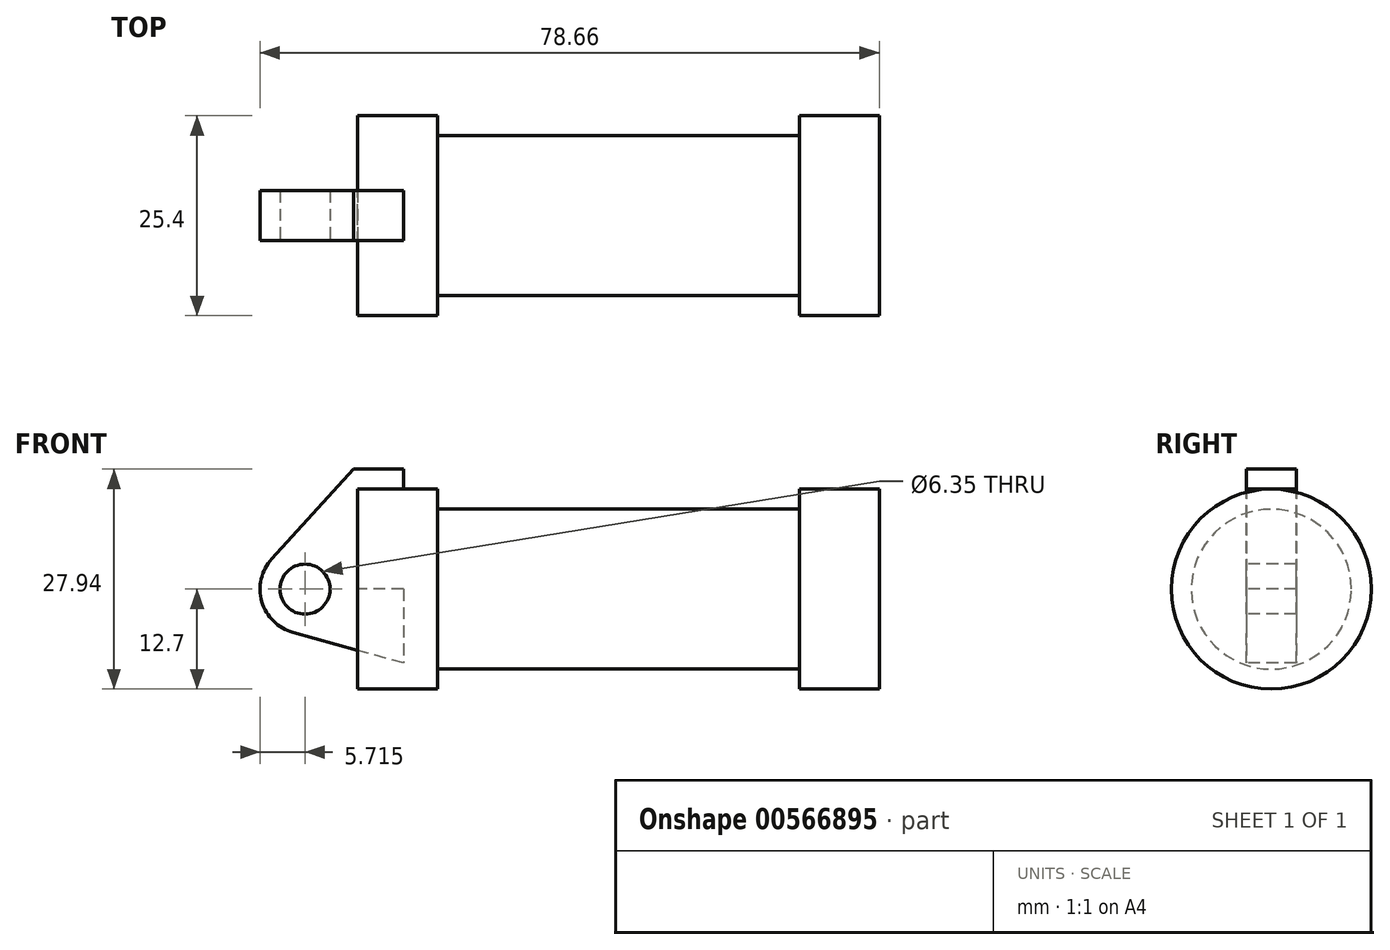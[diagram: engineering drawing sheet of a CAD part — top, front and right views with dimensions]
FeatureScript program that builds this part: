
annotation { "Feature Type Name" : "Feature", "Feature Type Description" : "" }
export const myFeature = defineFeature(function(context is Context, id is Id, definition is map)
    precondition{}
    {
        {
            var Q0;
            Q0=qCreatedBy(makeId("Front.planeOp"),FACE);
            var sketch = newSketch(context, id + "F0", { "sketchPlane" : qUnion([Q0])});
            skLineSegment(sketch, "E0", {"start": v(0, 0) * mm, "end": v(0, 12.7) * mm});
            skLineSegment(sketch, "E1", {"start": v(0, 12.7) * mm, "end": v(10.16, 12.7) * mm});
            skLineSegment(sketch, "E2", {"start": v(10.16, 12.7) * mm, "end": v(10.16, 10.16) * mm});
            skLineSegment(sketch, "E3", {"start": v(10.16, 10.16) * mm, "end": v(56.13, 10.16) * mm});
            skLineSegment(sketch, "E4", {"start": v(56.13, 10.16) * mm, "end": v(56.13, 12.7) * mm});
            skLineSegment(sketch, "E5", {"start": v(56.13, 12.7) * mm, "end": v(66.3, 12.7) * mm});
            skLineSegment(sketch, "E6", {"start": v(66.3, 12.7) * mm, "end": v(66.3, 0) * mm});
            skLineSegment(sketch, "E7", {"start": v(66.3, 0) * mm, "end": v(0, 0) * mm});
            skLineSegment(sketch, "E8", {"start": v(5.84, 15.24) * mm, "end": v(-0.5, 15.24) * mm});
            skLineSegment(sketch, "E9", {"start": v(-0.5, 15.24) * mm, "end": v(-10.88, 3.85) * mm});
            skLineSegment(sketch, "E10", {"start": v(0, 0) * mm, "end": v(-6.65, 0) * mm});
            skCircle(sketch, "E11", {"center": v(-6.65, 0) * mm, "radius": 5.72 * mm});
            skCircle(sketch, "E12", {"center": v(-6.65, 0) * mm, "radius": 3.18 * mm});
            skLineSegment(sketch, "E13", {"start": v(5.84, 15.24) * mm, "end": v(5.84, -9.4) * mm});
            skLineSegment(sketch, "E14", {"start": v(5.84, -9.4) * mm, "end": v(-8.18, -5.5) * mm});
            skSolve(sketch);
        }
        {
            var Q0;
            {var subQ0=sQuery(id+"F0.wireOp",EDGE,"E0");Q0=makeQuery(id+"F0.imprint","IMPRINT",FACE,{"disambiguationData":[TD([[makeQuery(id+"F0.imprint","IMPRINT",EDGE,{"derivedFrom":subQ0}),-1.0]])]});}
            var Q1;
            {var subQ0=sQuery(id+"F0.wireOp",EDGE,"E2");Q1=makeQuery(id+"F0.imprint","IMPRINT",FACE,{"disambiguationData":[TD([[makeQuery(id+"F0.imprint","IMPRINT",EDGE,{"derivedFrom":subQ0}),-1.0]])]});}
            var Q2;
            Q2=sQuery(id+"F0.wireOp",EDGE,"E7");
            revolve(context, id + "F1", {"entities" : qUnion([Q0, Q1]), "axis" : qUnion([Q2]), "revolveType" : RevolveType.FULL});
        }
        {
            var Q0;
            {var subQ1=sQuery(id+"F0.wireOp",EDGE,"E0");Q0=makeQuery(id+"F0.imprint","IMPRINT",FACE,{"disambiguationData":[TD([[makeQuery(id+"F0.imprint","IMPRINT",EDGE,{"derivedFrom":subQ1}),1.0]])]});}
            var Q1;
            {var subQ0=sQuery(id+"F0.wireOp",EDGE,"E14");Q1=makeQuery(id+"F0.imprint","IMPRINT",FACE,{"disambiguationData":[TD([[makeQuery(id+"F0.imprint","IMPRINT",EDGE,{"derivedFrom":subQ0}),-1.0]])]});}
            var Q2;
            {var subQ5=sQuery(id+"F0.wireOp",EDGE,"E12");Q2=makeQuery(id+"F0.imprint","IMPRINT",FACE,{"disambiguationData":[TD([[makeQuery(id+"F0.imprint","IMPRINT",EDGE,{"derivedFrom":subQ5}),-1.0]])]});}
            extrude(context, id + "F2", {"entities" : qUnion([Q0, Q1, Q2]), "endBound" : BoundingType.SYMMETRIC, "oppositeDirection" : true, "depth" : 6.35 * mm, "offsetDistance" : 25.4 * mm});
        }
    });
